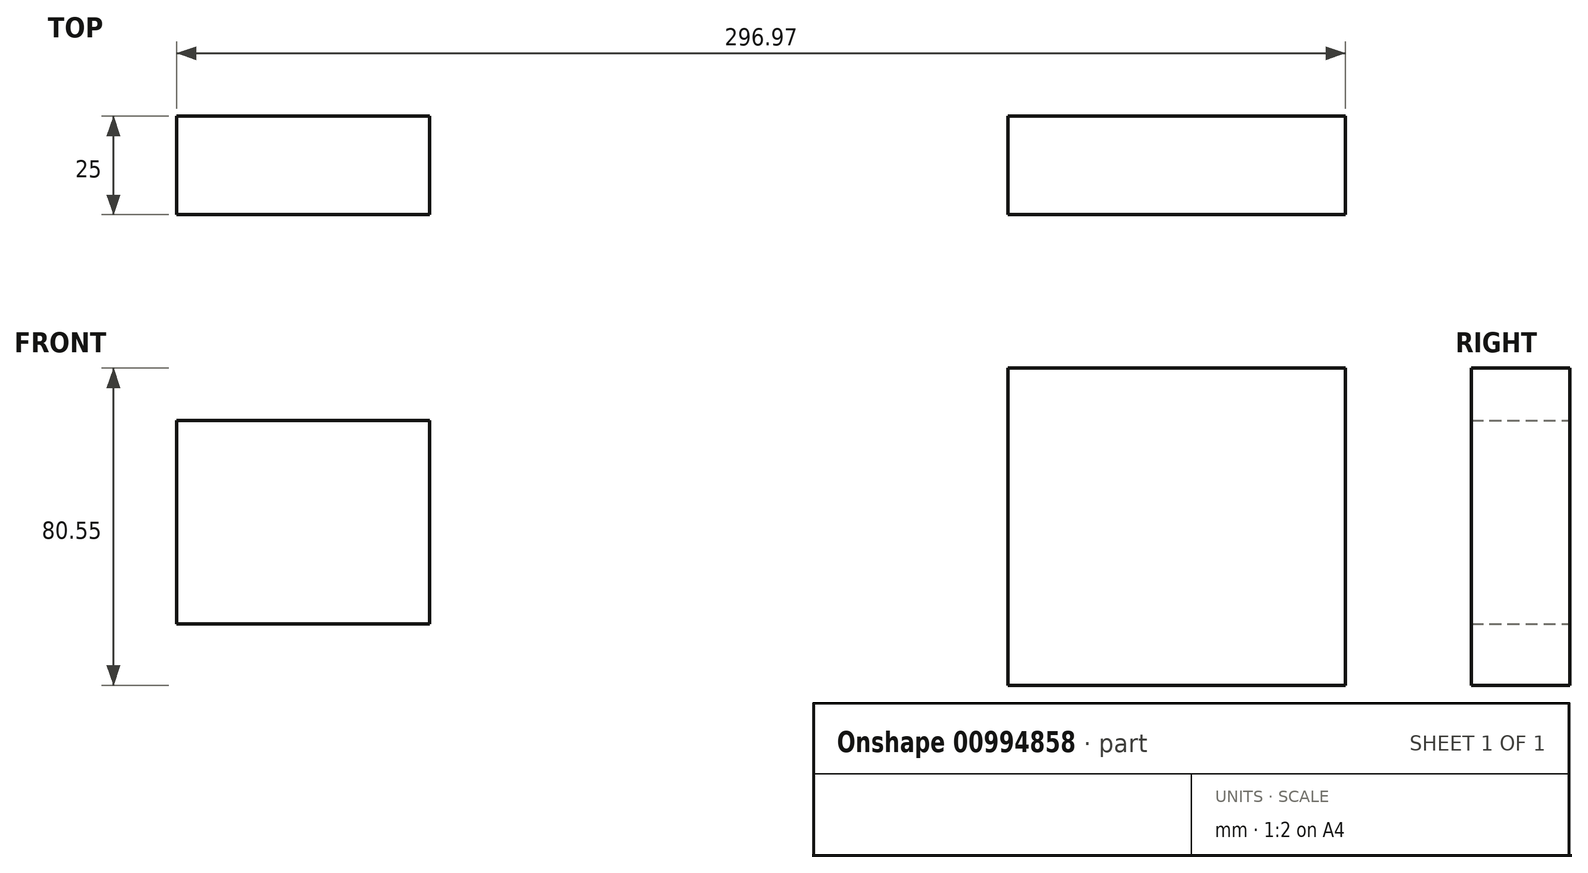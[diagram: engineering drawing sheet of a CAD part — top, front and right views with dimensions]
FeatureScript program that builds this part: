
annotation { "Feature Type Name" : "Feature", "Feature Type Description" : "" }
export const myFeature = defineFeature(function(context is Context, id is Id, definition is map)
    precondition{}
    {
        {
            var Q0;
            Q0=qCreatedBy(makeId("Front.planeOp"),FACE);
            var sketch = newSketch(context, id + "F0", { "sketchPlane" : qUnion([Q0])});
            skLineSegment(sketch, "E0.bottom", {"start": v(-134.85, 12.84) * mm, "end": v(-70.6, 12.84) * mm});
            skLineSegment(sketch, "E0.top", {"start": v(-134.85, 64.5) * mm, "end": v(-70.6, 64.5) * mm});
            skLineSegment(sketch, "E0.left", {"start": v(-134.85, 12.84) * mm, "end": v(-134.85, 64.5) * mm});
            skLineSegment(sketch, "E0.right", {"start": v(-70.6, 12.84) * mm, "end": v(-70.6, 64.5) * mm});
            skPoint(sketch, "E0.middle", {"position": v(-102.72, 38.67) * mm});
            skLineSegment(sketch, "E1.bottom", {"start": v(76.43, -2.76) * mm, "end": v(162.12, -2.76) * mm});
            skLineSegment(sketch, "E1.top", {"start": v(76.43, 77.8) * mm, "end": v(162.12, 77.8) * mm});
            skLineSegment(sketch, "E1.left", {"start": v(76.43, -2.76) * mm, "end": v(76.43, 77.8) * mm});
            skLineSegment(sketch, "E1.right", {"start": v(162.12, -2.76) * mm, "end": v(162.12, 77.8) * mm});
            skPoint(sketch, "E1.middle", {"position": v(119.28, 37.52) * mm});
            skSolve(sketch);
        }
        {
            var Q0;
            Q0 = qSketchRegion(id + "F0", true);
            extrude(context, id + "F1", {"entities" : qUnion([Q0]), "depth" : 25 * mm, "offsetDistance" : 25 * mm});
        }
    });
